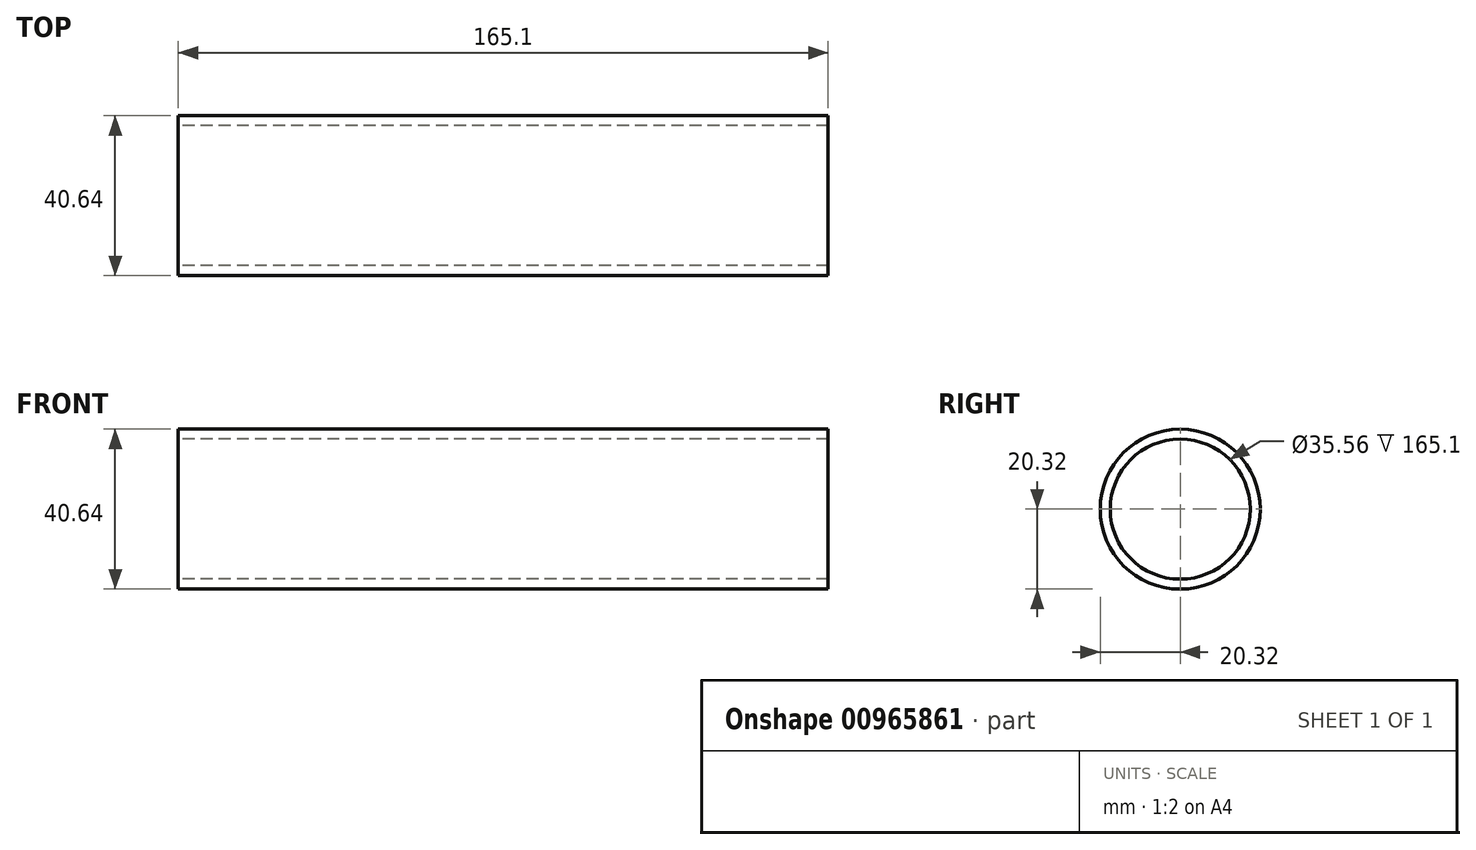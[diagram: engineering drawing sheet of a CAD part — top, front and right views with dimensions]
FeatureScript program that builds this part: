
annotation { "Feature Type Name" : "Feature", "Feature Type Description" : "" }
export const myFeature = defineFeature(function(context is Context, id is Id, definition is map)
    precondition{}
    {
        {
            var Q0;
            Q0=qCreatedBy(makeId("Right.planeOp"),FACE);
            var sketch = newSketch(context, id + "F0", { "sketchPlane" : qUnion([Q0])});
            skCircle(sketch, "E0", {"center": v(0, 0) * mm, "radius": 20.32 * mm});
            skCircle(sketch, "E1", {"center": v(0, 0) * mm, "radius": 17.78 * mm});
            skSolve(sketch);
        }
        {
            var Q0;
            Q0=makeQuery(id+"F0.imprint","IMPRINT",FACE,{"disambiguationData":[TD([[makeQuery(id+"F0.imprint","IMPRINT",EDGE,{"derivedFrom":sQuery(id+"F0.wireOp",EDGE,"E0")}),1.0]])]});
            extrude(context, id + "F1", {"entities" : qUnion([Q0]), "depth" : 165.1 * mm, "offsetDistance" : 25.4 * mm});
        }
    });
